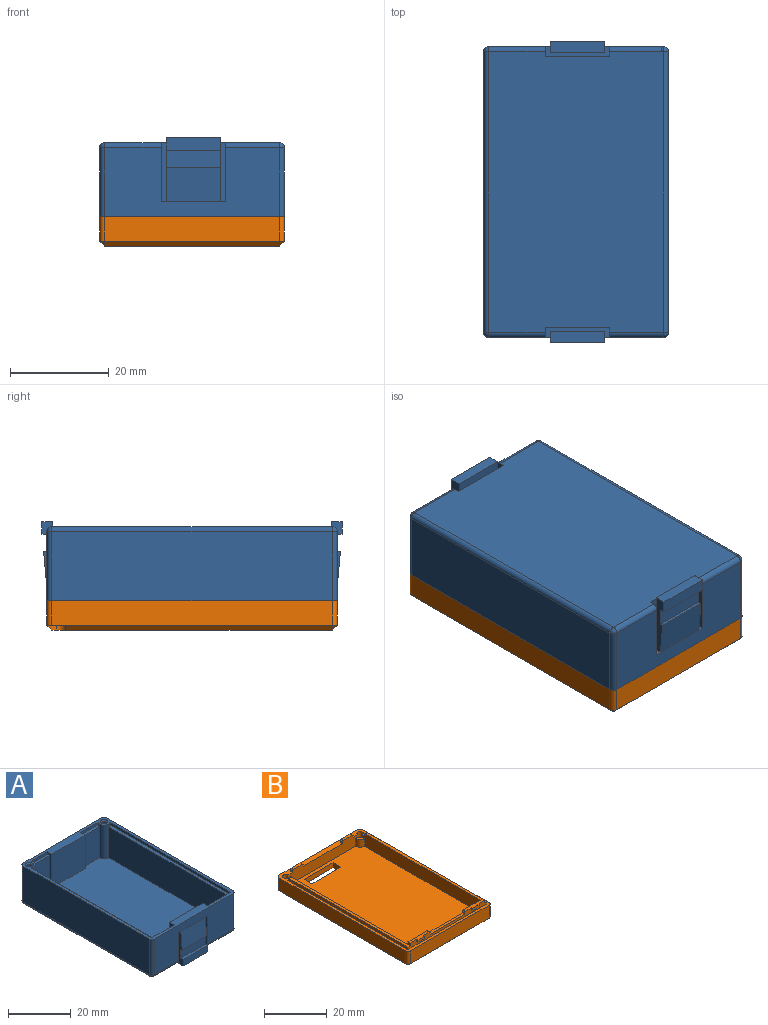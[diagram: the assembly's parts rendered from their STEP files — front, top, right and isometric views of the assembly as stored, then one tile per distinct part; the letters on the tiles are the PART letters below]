
ASSEMBLY  parts=2 mates=1
PART A: 90 faces, bbox 37.5x61x16 mm
  f0: plane 11x3.5mm, normal (0,1,0), area 38.5mm2, adj f44,f45,f47,f86
  f1: plane 10x2mm, normal (0,1,0), area 16mm2, adj f12,f23,f24,f55,f56,f57,f58,f77
  f2: plane 10.5x2mm, normal (0,1,0), area 16.5mm2, adj f12,f17,f26,f50,f51,f52,f53,f75
  f3: plane 35.5x14mm, normal (0,1,0), area 354mm2, adj f4,f9,f11,f12,f48,f60,f65,f66
  f4: plane 13x2mm, normal (0,0,-1), area 12.8mm2, adj f3,f9,f10,f11,f43,f44,f45
  f5: plane 11x3.5mm, normal (0,-1,0), area 38.5mm2, adj f36,f38,f40,f88
  f6: plane 12x2mm, normal (1,0,0), area 23.8mm2, adj f7,f15,f16,f27,f62
  f7: plane 13x12mm, normal (0,-1,0), area 156mm2, adj f6,f8,f16,f27
  f8: plane 12x2mm, normal (-1,0,0), area 23.8mm2, adj f7,f15,f16,f27,f63
  f9: plane 12x2mm, normal (-1,0,0), area 23.8mm2, adj f3,f4,f10,f16,f65
  f10: plane 13x12mm, normal (0,1,0), area 156mm2, adj f4,f9,f11,f16
  f11: plane 12x2mm, normal (1,0,0), area 23.8mm2, adj f3,f4,f10,f16,f60
  f12: plane 59x37.5mm, normal (0,0,1), area 255mm2, adj f1,f2,f3,f13,f14,f15,f17,f18
  f13: plane 57x14mm, normal (1,0,0), area 798mm2, adj f12,f64,f66,f72
  f14: plane 57x14mm, normal (-1,0,0), area 798mm2, adj f12,f61,f68,f70
  f15: plane 35.5x14mm, normal (0,-1,0), area 354mm2, adj f6,f8,f12,f27,f41,f62,f63,f70
  f16: plane 57x35.5mm, normal (0,0,-1), area 1997.5mm2, adj f6,f7,f8,f9,f10,f11,f60,f61
  f17: plane 54.27x1mm, normal (-1,0,0), area 54.3mm2, adj f2,f12,f28,f75
  f18: plane 7.77x1mm, normal (0,-1,0), area 7.8mm2, adj f12,f19,f28,f74
  f19: plane 13x2mm, normal (1,0,0), area 14mm2, adj f12,f18,f20,f74,f80,f84
  f20: plane 15x13mm, normal (0,-1,0), area 195mm2, adj f12,f19,f21,f84
  f21: plane 13x2mm, normal (-1,0,0), area 14mm2, adj f12,f20,f22,f76,f81,f84
  f22: plane 7.27x1mm, normal (0,-1,0), area 7.3mm2, adj f12,f21,f29,f76
  f23: plane 54.27x1mm, normal (1,0,0), area 54.3mm2, adj f1,f12,f29,f77
  f24: plane 13x2mm, normal (-1,0,0), area 15mm2, adj f1,f12,f25,f55,f83,f84
  f25: plane 15x13mm, normal (0,1,0), area 195mm2, adj f12,f24,f26,f84
  f26: plane 13x2mm, normal (1,0,0), area 15mm2, adj f2,f12,f25,f53,f78,f84
  f27: plane 13x2mm, normal (0,0,-1), area 12.8mm2, adj f6,f7,f8,f15,f36,f37,f38
  f28: cylinder r=2mm len=13mm, axis (0,0,-1), area 42.9mm2, adj f12,f17,f18,f74,f75,f79,f80,f84
  f29: cylinder r=2mm len=13mm, axis (0,0,-1), area 42.9mm2, adj f12,f22,f23,f76,f77,f81,f82,f84
  f30: cylinder r=0.7mm len=9.5mm, axis (0,0,1), area 41.8mm2, adj f31,f35
  f31: plane 1.4x1.4mm, normal (0,0,1), area 1.5mm2, adj f30
  f32: cylinder r=0.7mm len=9.5mm, axis (0,0,1), area 41.8mm2, adj f33,f34
  f33: plane 1.4x1.4mm, normal (0,0,1), area 1.5mm2, adj f32
  f34: cone r=0.7mm half-angle=45deg, axis (0,0,1), area 4.2mm2, adj f12,f32
  f35: cone r=0.7mm half-angle=45deg, axis (0,0,1), area 4.2mm2, adj f12,f30
  f36: plane 13x2.2mm, normal (-1,0,0), area 20.3mm2, adj f5,f27,f37,f39,f40,f41,f42,f88
  f37: plane 13x11mm, normal (0,1,0), area 143mm2, adj f27,f36,f38,f39
  f38: plane 13x2.2mm, normal (1,0,0), area 20.3mm2, adj f5,f27,f37,f39,f40,f41,f42,f88
  f39: plane 11x2.2mm, normal (0,0,-1), area 24.2mm2, adj f36,f37,f38,f89
  f40: plane 11x0.62mm, normal (0,0,-1), area 6.8mm2, adj f5,f36,f38,f42
  f41: plane 11x0.01mm, normal (0,0,1), area 0.1mm2, adj f15,f36,f38,f42
  f42: plane 11x7mm, normal (0,-1,0.09), area 77.3mm2, adj f36,f38,f40,f41
  f43: plane 13x11mm, normal (0,-1,0), area 143mm2, adj f4,f44,f45,f46
  f44: plane 13x2.2mm, normal (-1,0,0), area 20.3mm2, adj f0,f4,f43,f46,f47,f48,f49,f86
  f45: plane 13x2.2mm, normal (1,0,0), area 20.3mm2, adj f0,f4,f43,f46,f47,f48,f49,f86
  f46: plane 11x2.2mm, normal (0,0,-1), area 24.2mm2, adj f43,f44,f45,f87
  f47: plane 11x0.62mm, normal (0,0,-1), area 6.8mm2, adj f0,f44,f45,f49
  f48: plane 11x0.01mm, normal (0,0,1), area 0.1mm2, adj f3,f44,f45,f49
  f49: plane 11x7mm, normal (0,1,0.09), area 77.3mm2, adj f44,f45,f47,f48
  f50: plane 1x0.5mm, normal (1,0,0), area 0.5mm2, adj f2,f51,f53,f54
  f51: plane 3x0.5mm, normal (0,0,-1), area 1.5mm2, adj f2,f50,f52,f54
  f52: plane 1x0.5mm, normal (-1,0,0), area 0.5mm2, adj f2,f51,f53,f54
  f53: plane 9x1.5mm, normal (0,0,1), area 10.5mm2, adj f2,f26,f50,f52,f54,f78,f85
  f54: plane 3x1mm, normal (0,1,0), area 3mm2, adj f50,f51,f52,f53
  f55: plane 9x1.5mm, normal (0,0,1), area 10.5mm2, adj f1,f24,f56,f58,f59,f82,f83
  f56: plane 1x0.5mm, normal (1,0,0), area 0.5mm2, adj f1,f55,f57,f59
  f57: plane 3x0.5mm, normal (0,0,-1), area 1.5mm2, adj f1,f56,f58,f59
  f58: plane 1x0.5mm, normal (-1,0,0), area 0.5mm2, adj f1,f55,f57,f59
  f59: plane 3x1mm, normal (0,1,0), area 3mm2, adj f55,f56,f57,f58
  f60: cylinder r=1mm len=11mm, axis (-1,0,0), area 17.3mm2, adj f3,f11,f16,f69
  f61: cylinder r=1mm len=57mm, axis (0,-1,0), area 89.5mm2, adj f14,f16,f69,f71
  f62: cylinder r=1mm len=11mm, axis (1,0,0), area 17.3mm2, adj f6,f15,f16,f71
  f63: cylinder r=1mm len=11.5mm, axis (1,0,0), area 18.1mm2, adj f8,f15,f16,f73
  f64: cylinder r=1mm len=57mm, axis (0,1,0), area 89.5mm2, adj f13,f16,f67,f73
  f65: cylinder r=1mm len=11.5mm, axis (-1,0,0), area 18.1mm2, adj f3,f9,f16,f67
  f66: cylinder r=1mm len=14mm, axis (0,0,-1), area 22mm2, adj f3,f12,f13,f67
  f67: sphere r=1mm, area 1mm2, adj f64,f65,f66
  f68: cylinder r=1mm len=14mm, axis (0,0,1), area 22mm2, adj f3,f12,f14,f69
  f69: sphere r=1mm, area 2.1mm2, adj f60,f61,f68
  f70: cylinder r=1mm len=14mm, axis (0,0,-1), area 22mm2, adj f12,f14,f15,f71
  f71: sphere r=1mm, area 1.6mm2, adj f61,f62,f70
  f72: cylinder r=1mm len=14mm, axis (0,0,1), area 22mm2, adj f12,f13,f15,f73
  f73: sphere r=1mm, area 1.6mm2, adj f63,f64,f72
  f74: plane 7.77x1mm, normal (0,0,1), area 7.6mm2, adj f18,f19,f28,f80
  f75: plane 54.27x1.5mm, normal (0,0,1), area 54.6mm2, adj f2,f17,f28,f78,f79,f85
  f76: plane 7.27x1mm, normal (0,0,1), area 7.1mm2, adj f21,f22,f29,f81
  f77: plane 54.27x1mm, normal (0,0,1), area 54.1mm2, adj f1,f23,f29,f82
  f78: plane 12x9.5mm, normal (0,1,0), area 105mm2, adj f26,f53,f75,f79,f84,f85
  f79: plane 53x12mm, normal (-1,0,0), area 636mm2, adj f28,f75,f78,f84
  f80: plane 12x7.5mm, normal (0,-1,0), area 90mm2, adj f19,f28,f74,f84
  f81: plane 12x7mm, normal (0,-1,0), area 84mm2, adj f21,f29,f76,f84
  f82: plane 54x12mm, normal (1,0,0), area 637mm2, adj f1,f29,f55,f77,f83,f84
  f83: plane 11x9mm, normal (0,1,0), area 99mm2, adj f24,f55,f82,f84
  f84: plane 55x33.5mm, normal (0,0,1), area 1806.2mm2, adj f19,f20,f21,f24,f25,f26,f28,f29
  f85: plane 1x1mm, normal (-1,0,0), area 1mm2, adj f2,f53,f75,f78
  f86: plane 11x1mm, normal (0,0,1), area 11mm2, adj f0,f44,f45,f87
  f87: plane 11x2.5mm, normal (0,1,0), area 27.5mm2, adj f44,f45,f46,f86
  f88: plane 11x1mm, normal (0,0,1), area 11mm2, adj f5,f36,f38,f89
  f89: plane 11x2.5mm, normal (0,-1,0), area 27.5mm2, adj f36,f38,f39,f88
PART B: 77 faces, bbox 37.5x59x8 mm
  f0: plane 55x33.5mm, normal (0,0,1), area 1790.7mm2, adj f10,f13,f14,f20,f22,f24,f73,f74
  f1: plane 35.5x5mm, normal (0,1,0), area 177.5mm2, adj f15,f56,f60,f63,f64,f72
  f2: plane 57x35.5mm, normal (0,0,-1), area 1961.7mm2, adj f55,f57,f58,f59,f61,f62,f67,f69
  f3: plane 53.5x1mm, normal (0,0,1), area 53.5mm2, adj f9,f10,f19,f37,f46
  f4: plane 53.51x1mm, normal (0,0,1), area 53.5mm2, adj f6,f14,f19,f33,f44
  f5: plane 15.5x1mm, normal (0,0,1), area 15.5mm2, adj f19,f20,f34,f36
  f6: plane 54x1mm, normal (1,0,0), area 53.9mm2, adj f4,f15,f19,f29,f44
  f7: plane 5x1mm, normal (0,1,0), area 4.9mm2, adj f11,f15,f27,f31,f41,f45
  f8: plane 5x1mm, normal (0,1,0), area 4.9mm2, adj f12,f15,f28,f30,f42,f43
  f9: plane 54x1mm, normal (-1,0,0), area 53.9mm2, adj f3,f15,f19,f32,f46
  f10: plane 54x5mm, normal (1,0,0), area 265.9mm2, adj f0,f3,f15,f20,f21,f22,f23,f32
  f11: plane 4x1mm, normal (0,0,1), area 4mm2, adj f7,f13,f41,f45
  f12: plane 4x1mm, normal (0,0,1), area 4mm2, adj f8,f13,f42,f43
  f13: plane 31.5x5mm, normal (0,-1,0), area 129.8mm2, adj f0,f11,f12,f15,f21,f22,f23,f24
  f14: plane 54x5mm, normal (-1,0,0), area 266mm2, adj f0,f4,f15,f20,f24,f25,f26,f29
  f15: plane 59x37.5mm, normal (0,0,1), area 212.9mm2, adj f1,f6,f7,f8,f9,f10,f13,f14
  f16: plane 57x5mm, normal (1,0,0), area 285mm2, adj f15,f60,f63,f66,f67
  f17: plane 57x5mm, normal (-1,0,0), area 285mm2, adj f15,f56,f64,f65,f70
  f18: plane 35.5x5mm, normal (0,-1,0), area 177.5mm2, adj f15,f65,f66,f69
  f19: plane 35.5x2mm, normal (0,-1,0), area 47.4mm2, adj f3,f4,f5,f6,f9,f15,f33,f34
  f20: plane 33.5x6mm, normal (0,1,0), area 185.4mm2, adj f0,f5,f10,f14,f33,f34,f35,f36
  f21: cylinder r=1mm len=5mm, axis (0,0,-1), area 29.8mm2, adj f10,f13,f15,f23,f56
  f22: cylinder r=2mm len=3mm, axis (0,0,-1), area 9.4mm2, adj f0,f10,f13,f23
  f23: plane 2x2mm, normal (0,0,1), area 2.4mm2, adj f10,f13,f21,f22
  f24: cylinder r=2mm len=3mm, axis (0,0,-1), area 9.4mm2, adj f0,f13,f14,f26
  f25: cylinder r=1mm len=5mm, axis (0,0,-1), area 29.8mm2, adj f13,f14,f15,f26,f60
  f26: plane 2x2mm, normal (0,0,1), area 2.4mm2, adj f13,f14,f24,f25
  f27: plane 1x0.5mm, normal (1,0,0), area 0.5mm2, adj f7,f13,f15,f41
  f28: plane 1x0.5mm, normal (-1,0,0), area 0.5mm2, adj f8,f13,f15,f42
  f29: plane 1x0.5mm, normal (0.01,1,0), area 0.5mm2, adj f6,f14,f15,f44
  f30: plane 1x0.5mm, normal (1,0,0), area 0.5mm2, adj f8,f13,f15,f43
  f31: plane 1x0.5mm, normal (-1,0,0), area 0.5mm2, adj f7,f13,f15,f45
  f32: plane 1x0.5mm, normal (0,1,0), area 0.5mm2, adj f9,f10,f15,f46
  f33: plane 1x1mm, normal (1,0,0), area 1mm2, adj f4,f19,f20,f35
  f34: plane 1x0.5mm, normal (-1,0,0), area 0.5mm2, adj f5,f19,f20,f39
  f35: plane 8.5x1.5mm, normal (0,0,1), area 10mm2, adj f19,f20,f33,f39,f47,f49,f50
  f36: plane 1x0.5mm, normal (1,0,0), area 0.5mm2, adj f5,f19,f20,f40
  f37: plane 1x1mm, normal (-1,0,0), area 1mm2, adj f3,f19,f20,f38
  f38: plane 8.5x1.5mm, normal (0,0,1), area 10mm2, adj f19,f20,f37,f40,f51,f53,f54
  f39: cylinder r=0.5mm len=1mm, axis (0,1,0), area 0.8mm2, adj f19,f20,f34,f35
  f40: cylinder r=0.5mm len=1mm, axis (0,-1,0), area 0.8mm2, adj f19,f20,f36,f38
  f41: cylinder r=0.5mm len=1mm, axis (0,1,0), area 0.8mm2, adj f7,f11,f13,f27
  f42: cylinder r=0.5mm len=1mm, axis (0,-1,0), area 0.8mm2, adj f8,f12,f13,f28
  f43: cylinder r=0.5mm len=1mm, axis (0,1,0), area 0.8mm2, adj f8,f12,f13,f30
  f44: cylinder r=0.5mm len=1.01mm, axis (-1,0.01,0), area 0.8mm2, adj f4,f6,f14,f29
  f45: cylinder r=0.5mm len=1mm, axis (0,-1,0), area 0.8mm2, adj f7,f11,f13,f31
  f46: cylinder r=0.5mm len=1mm, axis (-1,0,0), area 0.8mm2, adj f3,f9,f10,f32
  f47: plane 1x0.5mm, normal (-1,0,0), area 0.5mm2, adj f19,f35,f48,f50
  f48: plane 3x0.5mm, normal (0,0,-1), area 1.5mm2, adj f19,f47,f49,f50
  f49: plane 1x0.5mm, normal (1,0,0), area 0.5mm2, adj f19,f35,f48,f50
  f50: plane 3x1mm, normal (0,-1,0), area 3mm2, adj f35,f47,f48,f49
  f51: plane 1x0.5mm, normal (-1,0,0), area 0.5mm2, adj f19,f38,f52,f54
  f52: plane 3x0.5mm, normal (0,0,-1), area 1.5mm2, adj f19,f51,f53,f54
  f53: plane 1x0.5mm, normal (1,0,0), area 0.5mm2, adj f19,f38,f52,f54
  f54: plane 3x1mm, normal (0,-1,0), area 3mm2, adj f38,f51,f52,f53
  f55: cylinder r=2mm len=2.03mm, axis (0,0,-1), area 3.2mm2, adj f2,f56,f57,f58
  f56: plane 4x4mm, normal (0,0,-1), area 11.8mm2, adj f1,f17,f21,f55,f57,f58,f64
  f57: plane 1.97x1mm, normal (0,1,0), area 1.5mm2, adj f2,f55,f56,f70
  f58: plane 2x1mm, normal (-1,0,0), area 1.5mm2, adj f2,f55,f56,f72
  f59: cylinder r=2mm len=2mm, axis (0,0,-1), area 3.1mm2, adj f2,f60,f61,f62
  f60: plane 4x4mm, normal (0,0,-1), area 11.8mm2, adj f1,f16,f25,f59,f61,f62,f63
  f61: plane 2x1mm, normal (1,0,0), area 1.5mm2, adj f2,f59,f60,f72
  f62: plane 2x1mm, normal (0,1,0), area 1.5mm2, adj f2,f59,f60,f67
  f63: cylinder r=1mm len=5mm, axis (0,0,-1), area 7.9mm2, adj f1,f15,f16,f60
  f64: cylinder r=1mm len=5mm, axis (0,0,1), area 7.9mm2, adj f1,f15,f17,f56
  f65: cylinder r=1mm len=5mm, axis (0,0,-1), area 7.9mm2, adj f15,f17,f18,f71
  f66: cylinder r=1mm len=5mm, axis (0,0,1), area 7.9mm2, adj f15,f16,f18,f68
  f67: plane 54x1mm, normal (0.71,0,-0.71), area 76.4mm2, adj f2,f16,f62,f68
  f68: cone r=1mm half-angle=45deg, axis (0,0,1), area 1.1mm2, adj f66,f67,f69
  f69: plane 35.5x1mm, normal (0,-0.71,-0.71), area 50.2mm2, adj f2,f18,f68,f71
  f70: plane 54x1mm, normal (-0.71,0,-0.71), area 76.4mm2, adj f2,f17,f57,f71
  f71: cone r=1mm half-angle=45deg, axis (0,0,1), area 1.1mm2, adj f65,f69,f70
  f72: plane 29.5x1mm, normal (0,0.71,-0.71), area 41.7mm2, adj f1,f2,f58,f61
  f73: plane 3.5x2mm, normal (-1,0,0), area 7mm2, adj f0,f2,f74,f76
  f74: plane 13x2mm, normal (0,1,0), area 26mm2, adj f0,f2,f73,f75
  f75: plane 3.5x2mm, normal (1,0,0), area 7mm2, adj f0,f2,f74,f76
  f76: plane 13x2mm, normal (0,-1,0), area 26mm2, adj f0,f2,f73,f75
PLACE A rot(axis=(0,1,0),180deg) t=(52.76,23.5,8.95)mm
PLACE B t=(54.58,26.44,-12.05)mm
MATE fastened A.f12 <-> B.f15  axis (0,0,-1) through (72.58,55.94,-6.05)mm
